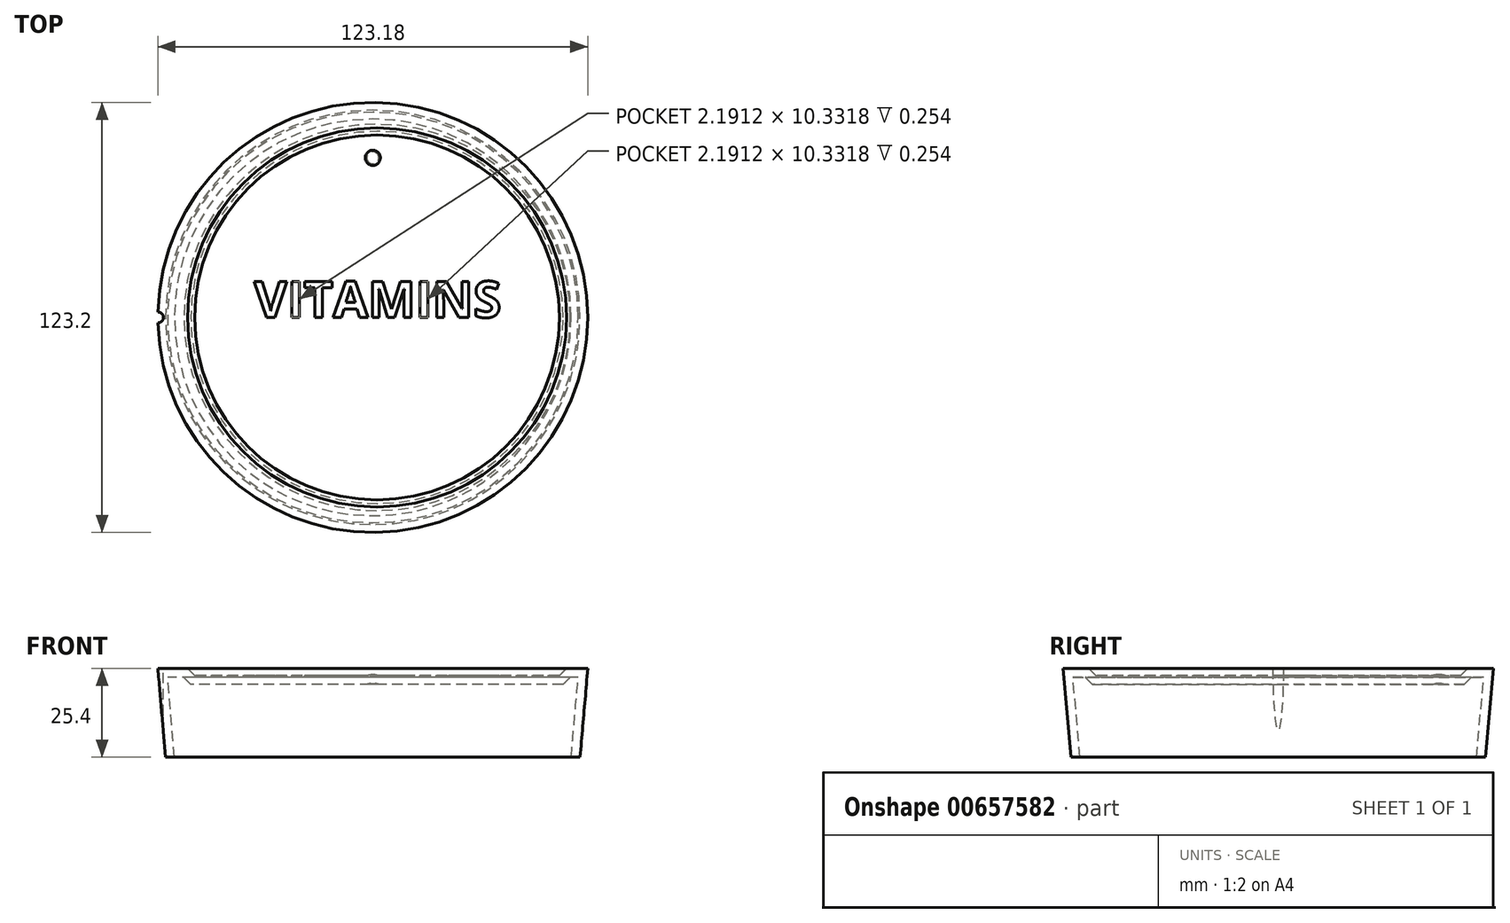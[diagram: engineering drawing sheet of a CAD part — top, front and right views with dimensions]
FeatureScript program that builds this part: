
annotation { "Feature Type Name" : "Feature", "Feature Type Description" : "" }
export const myFeature = defineFeature(function(context is Context, id is Id, definition is map)
    precondition{}
    {
        {
            var Q0;
            Q0=qCreatedBy(makeId("Top.planeOp"),FACE);
            var sketch = newSketch(context, id + "F0", { "sketchPlane" : qUnion([Q0])});
            skCircle(sketch, "E0", {"center": v(0, 0) * mm, "radius": 59.38 * mm});
            skSolve(sketch);
        }
        {
            var Q0;
            Q0 = qSketchRegion(id + "F0", true);
            extrude(context, id + "F1", {"entities" : qUnion([Q0]), "depth" : 25.4 * mm, "offsetDistance" : 25.4 * mm, "hasDraft" : true, "draftAngle" : 5 * degree});
        }
        {
            var Q0;
            Q0=makeQuery(id+"F1.opExtrude","CAP_FACE",FACE,{"disambiguationData":[OSD([sQuery(id+"F0.wireOp",EDGE,"E0")])],"isStart":false});
            var sketch = newSketch(context, id + "F2", { "sketchPlane" : qUnion([Q0])});
            skCircle(sketch, "E1", {"center": v(1.2, 0) * mm, "radius": 57.35 * mm});
            skSolve(sketch);
        }
        {
            var Q0;
            Q0 = qSketchRegion(id + "F2", true);
            extrude(context, id + "F3", {"entities" : qUnion([Q0]), "operationType" : NewBodyOperationType.REMOVE, "oppositeDirection" : true, "depth" : 2.03 * mm, "offsetDistance" : 25.4 * mm});
        }
        {
            var Q0;
            Q0=makeQuery(id+"F3.boolean.opBoolean","COPY",EDGE,{"derivedFrom":makeQuery(id+"F3.opExtrude","CAP_EDGE",EDGE,{"disambiguationData":[OSD([sQuery(id+"F2.wireOp",EDGE,"E1")])],"isStart":false})});
            chamfer(context, id + "F4", {"entities" : qUnion([Q0]), "width" : 5.08 * mm, "tangentPropagation" : true});
        }
        {
            var Q0;
            Q0=qCreatedBy(makeId("Front.planeOp"),FACE);
            var sketch = newSketch(context, id + "F5", { "sketchPlane" : qUnion([Q0])});
            skLineSegment(sketch, "E2", {"start": v(0, 0) * mm, "end": v(0, 45.27) * mm, "construction": true});
            skSolve(sketch);
        }
        {
            var Q0;
            Q0=makeQuery(id+"F3.boolean.opBoolean","COPY",FACE,{"derivedFrom":makeQuery(id+"F3.opExtrude","CAP_FACE",FACE,{"disambiguationData":[OSD([sQuery(id+"F2.wireOp",EDGE,"E1")])],"isStart":false})});
            var sketch = newSketch(context, id + "F6", { "sketchPlane" : qUnion([Q0])});
            skCircle(sketch, "E3", {"center": v(0, 45.74) * mm, "radius": 2.17 * mm});
            skSolve(sketch);
        }
        {
            var Q0;
            Q0 = qSketchRegion(id + "F6", true);
            extrude(context, id + "F7", {"entities" : qUnion([Q0]), "operationType" : NewBodyOperationType.ADD, "depth" : 0.23 * mm, "offsetDistance" : 25.4 * mm});
        }
        {
            var Q0;
            Q0=makeQuery(id+"F3.boolean.opBoolean","COPY",FACE,{"derivedFrom":makeQuery(id+"F3.opExtrude","CAP_FACE",FACE,{"disambiguationData":[OSD([sQuery(id+"F2.wireOp",EDGE,"E1")])],"isStart":false})});
            var sketch = newSketch(context, id + "F8", { "sketchPlane" : qUnion([Q0])});
            skText(sketch, "E4", { "text": "VITAMINS\n", "fontName": "OpenSans-Bold.ttf"});
            const initialGuessF8  = {"E4": [-0.03396, 0, 1, 0, 0.01042]};
            skSetInitialGuess(sketch, initialGuessF8);
            skSolve(sketch);
        }
        {
            var Q0;
            Q0=makeQuery(id+"F7.opExtrude","CAP_EDGE",EDGE,{"disambiguationData":[OSD([sQuery(id+"F6.wireOp",EDGE,"E3")])],"isStart":false});
            fillet(context, id + "F9", {"entities" : qUnion([Q0]), "radius" : 5.08 * mm, "tangentPropagation" : true, "allowEdgeOverflow" : false});
        }
        {
            var Q0;
            Q0=makeQuery(id+"F1.opExtrude","CAP_FACE",FACE,{"disambiguationData":[OSD([sQuery(id+"F0.wireOp",EDGE,"E0")])],"isStart":true});
            shell(context, id + "F10", {"entities" : qUnion([Q0]), "thickness" : 2.54 * mm});
        }
        {
            var Q0;
            Q0 = qSketchRegion(id + "F8", true);
            extrude(context, id + "F11", {"entities" : qUnion([Q0]), "operationType" : NewBodyOperationType.REMOVE, "oppositeDirection" : true, "depth" : 0.25 * mm, "offsetDistance" : 25.4 * mm});
        }
        {
            var Q0;
            Q0=makeQuery(id+"F1.opExtrude","CAP_FACE",FACE,{"disambiguationData":[OSD([sQuery(id+"F0.wireOp",EDGE,"E0")])],"isStart":false});
            var sketch = newSketch(context, id + "F12", { "sketchPlane" : qUnion([Q0])});
            skCircle(sketch, "E5", {"center": v(-61.6, 0) * mm, "radius": 1.58 * mm});
            skSolve(sketch);
        }
        {
            var Q0;
            Q0 = qSketchRegion(id + "F12", true);
            extrude(context, id + "F13", {"entities" : qUnion([Q0]), "operationType" : NewBodyOperationType.REMOVE, "oppositeDirection" : true, "depth" : 25.4 * mm, "offsetDistance" : 25.4 * mm});
        }
    });
